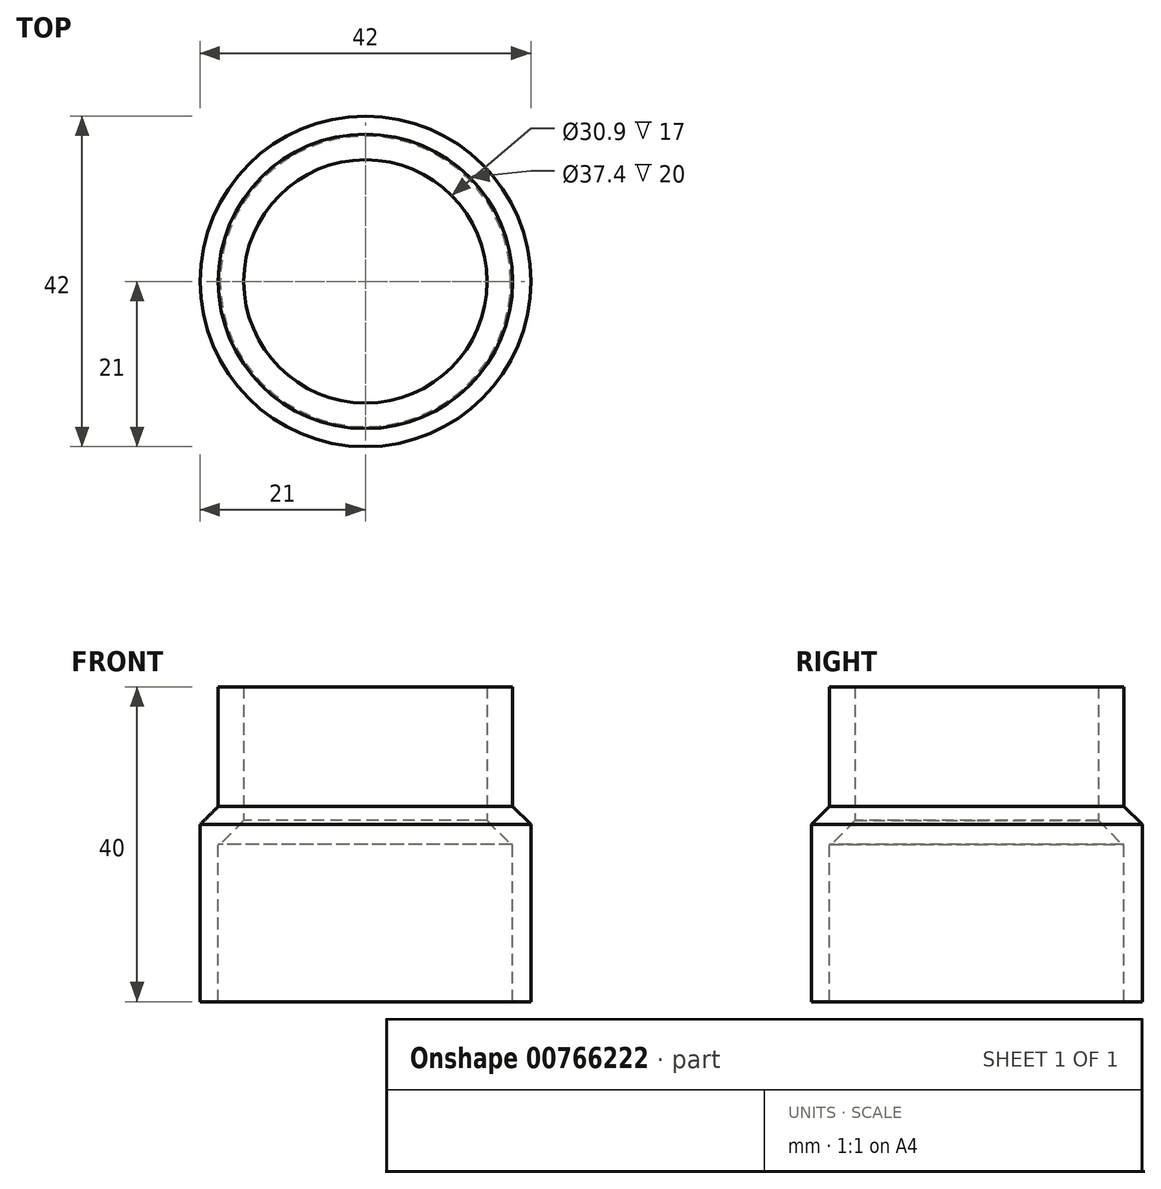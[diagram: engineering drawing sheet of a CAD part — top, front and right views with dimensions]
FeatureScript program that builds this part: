
annotation { "Feature Type Name" : "Feature", "Feature Type Description" : "" }
export const myFeature = defineFeature(function(context is Context, id is Id, definition is map)
    precondition{}
    {
        {
            var Q0;
            Q0=qCreatedBy(makeId("Top.planeOp"),FACE);
            var sketch = newSketch(context, id + "F0", { "sketchPlane" : qUnion([Q0])});
            skCircle(sketch, "E0", {"center": v(0, 0) * mm, "radius": 18.7 * mm});
            skCircle(sketch, "E1", {"center": v(0, 0) * mm, "radius": 15.45 * mm});
            skCircle(sketch, "E2", {"center": v(0, 0) * mm, "radius": 21 * mm});
            skSolve(sketch);
        }
        {
            var Q0;
            Q0=makeQuery(id+"F0.imprint","IMPRINT",FACE,{"disambiguationData":[TD([[makeQuery(id+"F0.imprint","IMPRINT",EDGE,{"derivedFrom":sQuery(id+"F0.wireOp",EDGE,"E0")}),1.0]])]});
            extrude(context, id + "F1", {"entities" : qUnion([Q0]), "depth" : 20 * mm, "offsetDistance" : 25 * mm});
        }
        {
            var Q0;
            Q0=makeQuery(id+"F0.imprint","IMPRINT",FACE,{"disambiguationData":[TD([[makeQuery(id+"F0.imprint","IMPRINT",EDGE,{"derivedFrom":sQuery(id+"F0.wireOp",EDGE,"E0")}),-1.0]])]});
            extrude(context, id + "F2", {"entities" : qUnion([Q0]), "operationType" : NewBodyOperationType.ADD, "depth" : 5 * mm, "offsetDistance" : 25 * mm});
        }
        {
            var Q0;
            Q0=makeQuery(id+"F0.imprint","IMPRINT",FACE,{"disambiguationData":[TD([[makeQuery(id+"F0.imprint","IMPRINT",EDGE,{"derivedFrom":sQuery(id+"F0.wireOp",EDGE,"E0")}),-1.0]])]});
            extrude(context, id + "F3", {"entities" : qUnion([Q0]), "operationType" : NewBodyOperationType.ADD, "oppositeDirection" : true, "depth" : 20 * mm, "offsetDistance" : 25 * mm});
        }
        {
            var Q0;
            Q0=makeQuery(id+"F2.opExtrude","CAP_EDGE",EDGE,{"disambiguationData":[OSD([sQuery(id+"F0.wireOp",EDGE,"E2")])],"isStart":false});
            chamfer(context, id + "F4", {"entities" : qUnion([Q0]), "width" : 2.5 * mm, "tangentPropagation" : true});
        }
        {
            var Q0;
            Q0=makeQuery(id+"F1.opExtrude","CAP_EDGE",EDGE,{"disambiguationData":[OSD([sQuery(id+"F0.wireOp",EDGE,"E1")])],"isStart":true});
            chamfer(context, id + "F5", {"entities" : qUnion([Q0]), "width" : 3 * mm, "tangentPropagation" : true});
        }
    });
